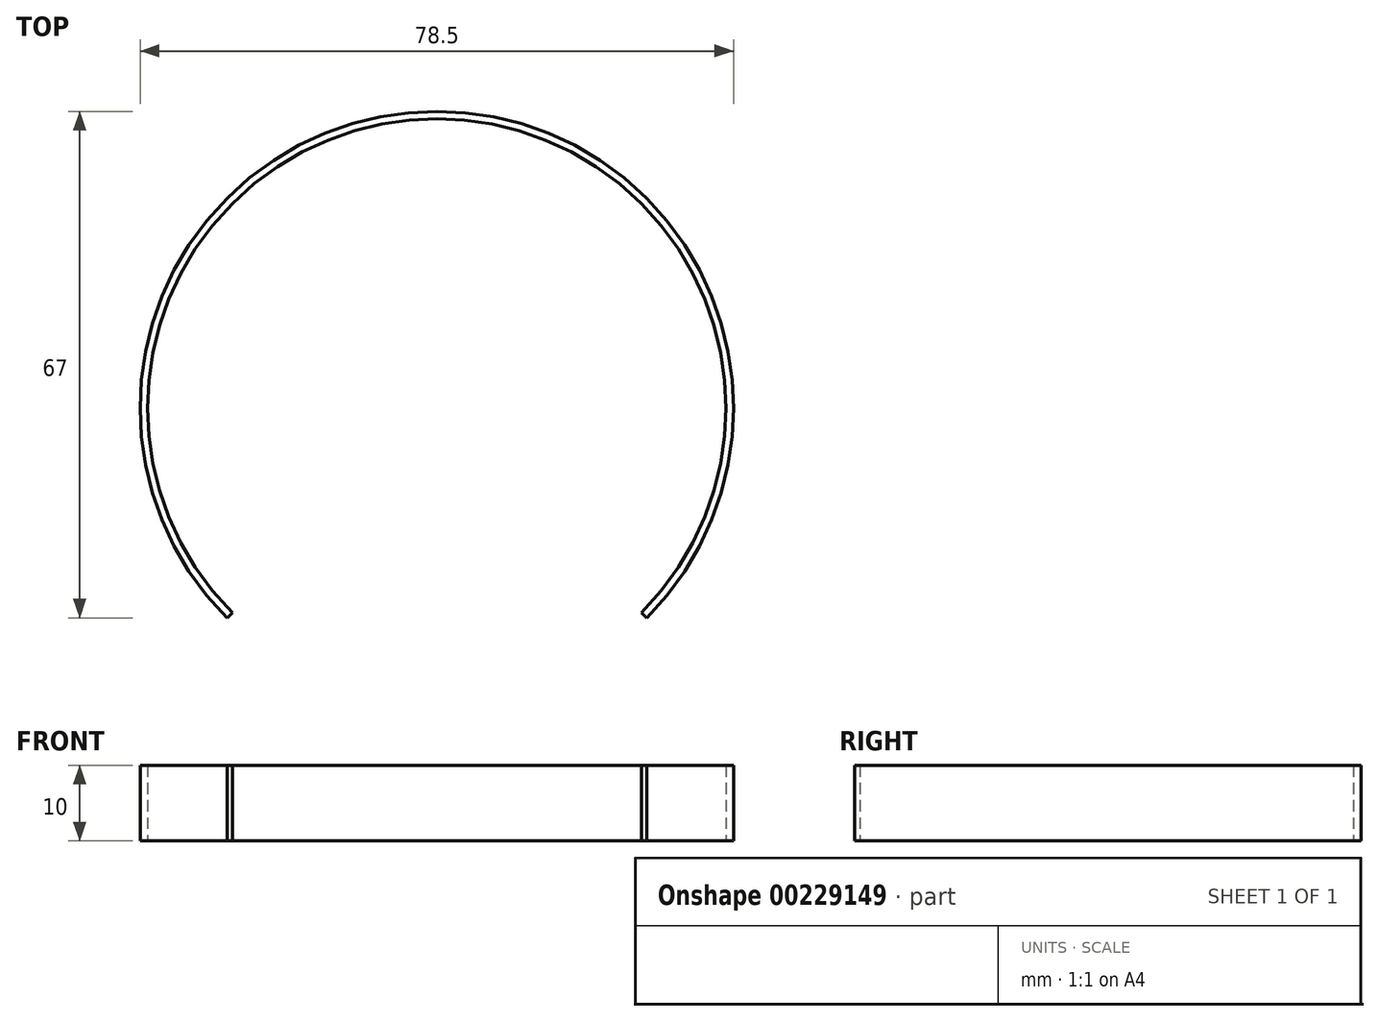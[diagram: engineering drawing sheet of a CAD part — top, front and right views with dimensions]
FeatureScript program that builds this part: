
annotation { "Feature Type Name" : "Feature", "Feature Type Description" : "" }
export const myFeature = defineFeature(function(context is Context, id is Id, definition is map)
    precondition{}
    {
        {
            var Q0;
            Q0=qCreatedBy(makeId("Top.planeOp"),FACE);
            var sketch = newSketch(context, id + "F0", { "sketchPlane" : qUnion([Q0])});
            skArc(sketch, "E0", {"start": v(27.05, -27.05) * mm, "mid": v(0, 38.25) * mm, "end": v(-27.05, -27.05) * mm});
            skArc(sketch, "E1", {"start": v(27.75, -27.75) * mm, "mid": v(0, 39.25) * mm, "end": v(-27.75, -27.75) * mm});
            skLineSegment(sketch, "E2", {"start": v(27.05, -27.05) * mm, "end": v(27.75, -27.75) * mm});
            skLineSegment(sketch, "E3", {"start": v(0, -60.58) * mm, "end": v(0, 54.66) * mm, "construction": true});
            skLineSegment(sketch, "E4.MirrorCS", {"start": v(-27.05, -27.05) * mm, "end": v(-27.75, -27.75) * mm});
            skSolve(sketch);
        }
        {
            var Q0;
            Q0 = qSketchRegion(id + "F0", true);
            extrude(context, id + "F1", {"entities" : qUnion([Q0]), "depth" : 10 * mm, "offsetDistance" : 25 * mm});
        }
    });
